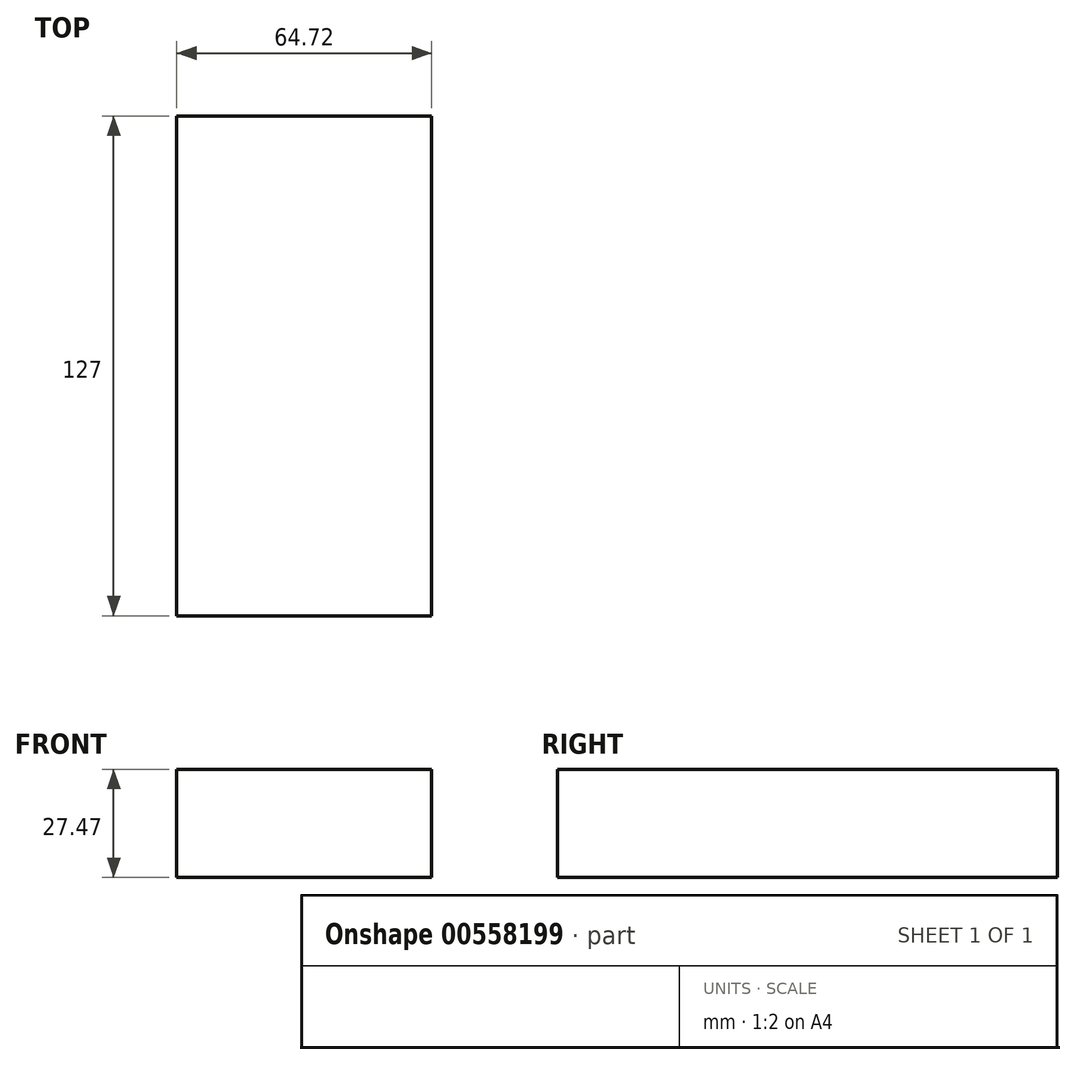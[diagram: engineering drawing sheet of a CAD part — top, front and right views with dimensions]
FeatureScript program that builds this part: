
annotation { "Feature Type Name" : "Feature", "Feature Type Description" : "" }
export const myFeature = defineFeature(function(context is Context, id is Id, definition is map)
    precondition{}
    {
        {
            var Q0;
            Q0=qCreatedBy(makeId("Front.planeOp"),FACE);
            var sketch = newSketch(context, id + "F0", { "sketchPlane" : qUnion([Q0])});
            skLineSegment(sketch, "E0.bottom", {"start": v(0, 6.26) * mm, "end": v(-64.72, 6.26) * mm});
            skLineSegment(sketch, "E0.top", {"start": v(0, 33.73) * mm, "end": v(-64.72, 33.73) * mm});
            skLineSegment(sketch, "E0.left", {"start": v(0, 6.26) * mm, "end": v(0, 33.73) * mm});
            skLineSegment(sketch, "E0.right", {"start": v(-64.72, 6.26) * mm, "end": v(-64.72, 33.73) * mm});
            skPoint(sketch, "E0.middle", {"position": v(-32.36, 20) * mm});
            skLineSegment(sketch, "E1", {"start": v(12.21, 45.03) * mm, "end": v(59.53, 30.37) * mm});
            skCircle(sketch, "E2", {"center": v(-43.96, 44.74) * mm, "radius": 11.01 * mm});
            skSolve(sketch);
        }
        {
            var Q0;
            Q0=makeQuery(id+"F0.imprint","IMPRINT",FACE,{"disambiguationData":[TD([[makeQuery(id+"F0.imprint","IMPRINT",EDGE,{"derivedFrom":sQuery(id+"F0.wireOp",EDGE,"E0.bottom")}),-1.0]])]});
            extrude(context, id + "F1", {"entities" : qUnion([Q0]), "endBound" : BoundingType.SYMMETRIC, "depth" : 127 * mm, "offsetDistance" : 25.4 * mm});
        }
    });
